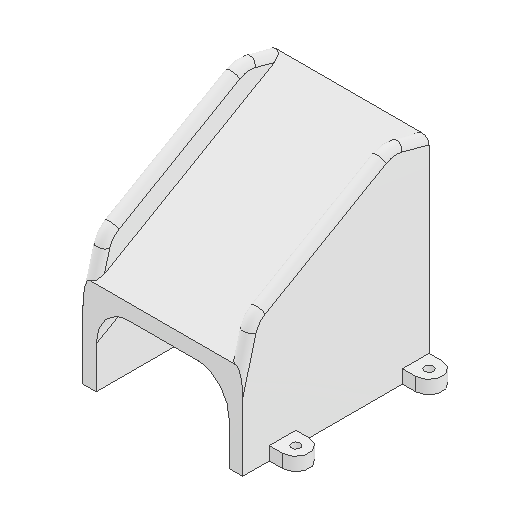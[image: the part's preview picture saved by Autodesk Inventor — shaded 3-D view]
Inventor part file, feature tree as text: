
AUTODESK INVENTOR PART (.ipt)
format: ipt  version: 2025 (Build 290162000, 162)  size: 196,608 bytes
history: native  units: mm
features: extrude x3, sketch x3, plane x3, mirror x3, fillet x3, hole x1, shell x1, chamfer x1
ambient origin geometry x8: Origin, YZ Plane, XZ Plane, XY Plane, X Axis, Y Axis, Z Axis, Center Point
bodies: Solid1 (feature_tree)
feature tree (18):
  extrude  "Extrusion1"  Depth=44.45mm
  sketch  "Sketch2"  dims[d2=30.0deg d3=76.2mm d4=0.0mm]
  plane  "Work Plane1"
  plane  "Work Plane2"
  extrude  "Extrusion2"  Depth=76.2mm TaperAngle=0.0deg
  hole  "Hole1"  [1 undecoded]
  plane  "Work Plane3"
  mirror  "Mirror1"
  mirror  "Mirror2"
  shell  "Shell1"  Thickness=6.35mm
  fillet  "Fillet2"  Radius=19.05mm
  extrude  "Extrusion3"  Depth=6.35mm
  chamfer  "Chamfer1"  Distance=6.35mm
  fillet  "Fillet3"  Radius=15.0mm
  fillet  "Fillet4"  Radius=6.35mm
  mirror  "Mirror3"
  sketch  "Sketch1"  dims[d0=88.9mm d1=44.45mm]
  sketch  "Sketch3"  dims[d5=44.45mm d6=12.7mm d7=6.35mm d8=0.0mm d9=4.25mm d10=6.0mm d11=4.0mm d12=2.0mm d13=90.0deg d14=8.0mm d15=20.594885mm d17=19.05mm d18=6.35mm d19=6.35mm d20=15.0mm d21=6.35mm d22=12.7mm d23=0.0mm d24=12.7mm d25=2.0mm d26=45.0deg d27=12.7mm d28=3.175mm]
note: 1 required parameter value undecoded (feature->parameter linkage not recoverable at this tier; creation-order binding heuristic only, values carry confidence <= 0.55)
